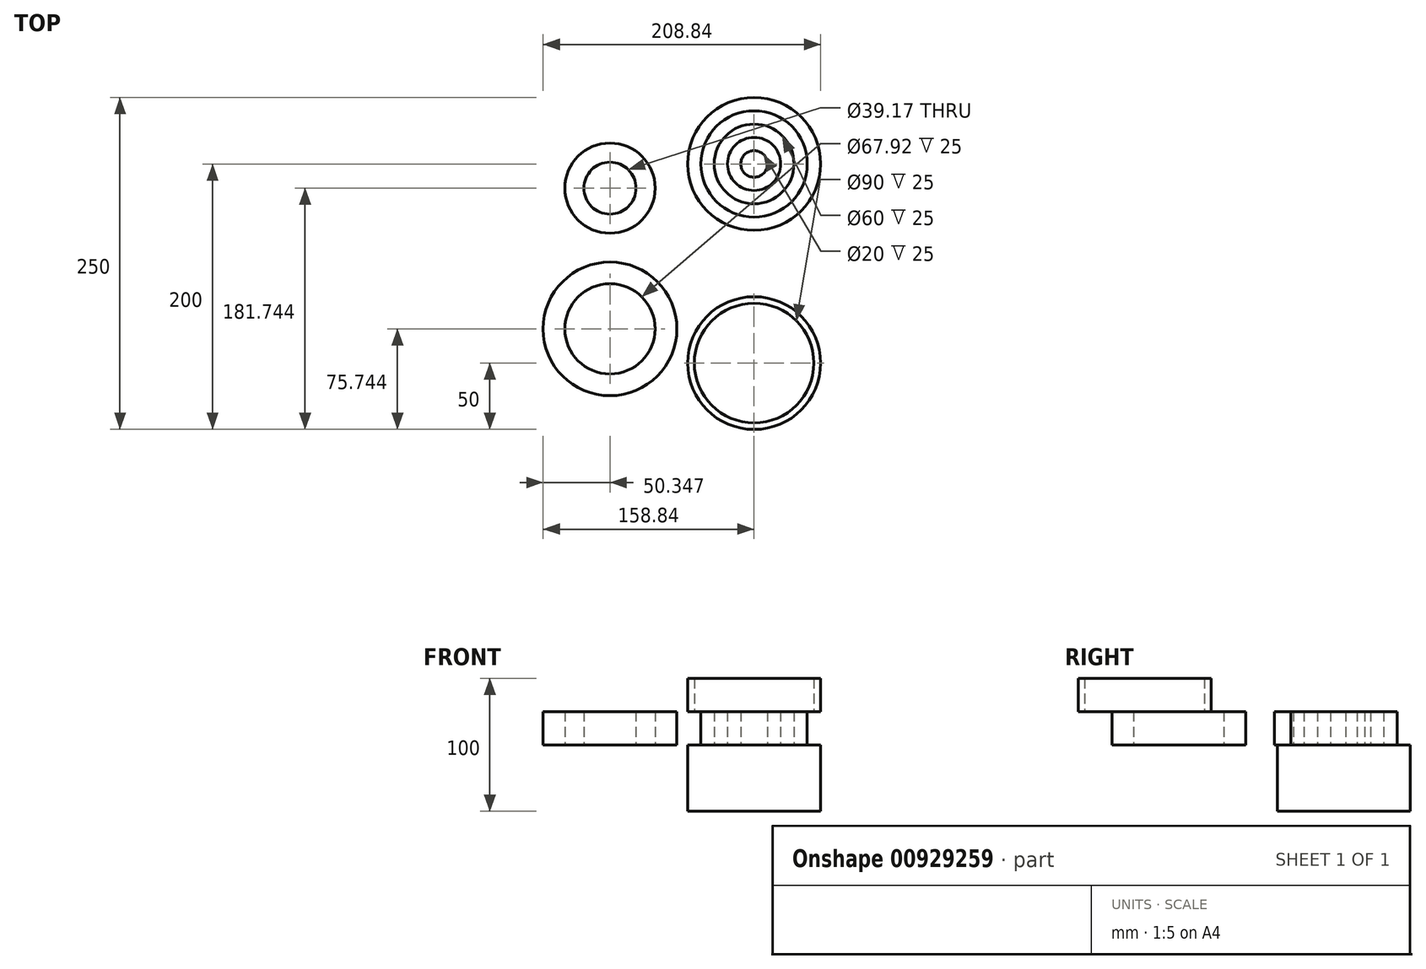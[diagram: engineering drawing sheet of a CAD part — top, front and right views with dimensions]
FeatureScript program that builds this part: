
annotation { "Feature Type Name" : "Feature", "Feature Type Description" : "" }
export const myFeature = defineFeature(function(context is Context, id is Id, definition is map)
    precondition{}
    {
        {
            var Q0;
            Q0=qCreatedBy(makeId("Top.planeOp"),FACE);
            var sketch = newSketch(context, id + "F0", { "sketchPlane" : qUnion([Q0])});
            skCircle(sketch, "E0", {"center": v(0, 0) * mm, "radius": 50 * mm});
            skSolve(sketch);
        }
        {
            var Q0;
            Q0 = qSketchRegion(id + "F0", true);
            extrude(context, id + "F1", {"entities" : qUnion([Q0]), "oppositeDirection" : true, "depth" : 50 * mm, "offsetDistance" : 25 * mm});
        }
        {
            var Q0;
            Q0=qCreatedBy(makeId("Top.planeOp"),FACE);
            var sketch = newSketch(context, id + "F2", { "sketchPlane" : qUnion([Q0])});
            skCircle(sketch, "E1", {"center": v(0, 0) * mm, "radius": 40 * mm});
            skCircle(sketch, "E2", {"center": v(0, 0) * mm, "radius": 30 * mm});
            skCircle(sketch, "E3", {"center": v(0, 0) * mm, "radius": 20 * mm});
            skCircle(sketch, "E4", {"center": v(0, 0) * mm, "radius": 10 * mm});
            skSolve(sketch);
        }
        {
            var Q0;
            Q0=makeQuery(id+"F2.imprint","IMPRINT",FACE,{"disambiguationData":[TD([[makeQuery(id+"F2.imprint","IMPRINT",EDGE,{"derivedFrom":sQuery(id+"F2.wireOp",EDGE,"E1")}),1.0]])]});
            var Q1;
            Q1=makeQuery(id+"F2.imprint","IMPRINT",FACE,{"disambiguationData":[TD([[makeQuery(id+"F2.imprint","IMPRINT",EDGE,{"derivedFrom":sQuery(id+"F2.wireOp",EDGE,"E3")}),1.0]])]});
            extrude(context, id + "F3", {"entities" : qUnion([Q0, Q1]), "operationType" : NewBodyOperationType.ADD, "depth" : 25 * mm, "offsetDistance" : 25 * mm});
        }
        {
            var Q0;
            Q0=makeQuery(id+"F3.opExtrude","CAP_FACE",FACE,{"disambiguationData":[OSD([sQuery(id+"F2.wireOp",EDGE,"E1"),sQuery(id+"F2.wireOp",EDGE,"E2")])],"isStart":false});
            var sketch = newSketch(context, id + "F4", { "sketchPlane" : qUnion([Q0])});
            skCircle(sketch, "E5.0", {"center": v(0, 0) * mm, "radius": 45 * mm});
            skCircle(sketch, "E6.0", {"center": v(0, 0) * mm, "radius": 50 * mm});
            skSolve(sketch);
        }
        {
            var Q0;
            Q0 = qSketchRegion(id + "F4", true);
            extrude(context, id + "F5", {"entities" : qUnion([Q0]), "depth" : 25 * mm, "offsetDistance" : 25 * mm});
        }
        {
            var Q0;
            Q0=qCreatedBy(makeId("Top.planeOp"),FACE);
            var sketch = newSketch(context, id + "F6", { "sketchPlane" : qUnion([Q0])});
            skCircle(sketch, "E7", {"center": v(-108.5, -124.26) * mm, "radius": 33.96 * mm});
            skCircle(sketch, "E8", {"center": v(-108.5, -124.26) * mm, "radius": 19.58 * mm});
            skCircle(sketch, "E9", {"center": v(-108.5, -124.26) * mm, "radius": 50.35 * mm});
            skSolve(sketch);
        }
        {
            var Q0;
            Q0=makeQuery(id+"F6.imprint","IMPRINT",FACE,{"disambiguationData":[TD([[makeQuery(id+"F6.imprint","IMPRINT",EDGE,{"derivedFrom":sQuery(id+"F6.wireOp",EDGE,"E7")}),-1.0]])]});
            extrude(context, id + "F7", {"entities" : qUnion([Q0]), "operationType" : NewBodyOperationType.ADD, "depth" : 25 * mm, "offsetDistance" : 25 * mm});
        }
        {
            var Q0;
            Q0=makeQuery(id+"F7.opExtrude","SWEPT_BODY",BODY,{"disambiguationData":[OSD([sQuery(id+"F6.wireOp",EDGE,"E7"),sQuery(id+"F6.wireOp",EDGE,"E9")])]});
            deleteBodies(context, id + "F8", {"entities" : qUnion([Q0])});
        }
        {
            var Q0;
            Q0=makeQuery(id+"F6.imprint","IMPRINT",FACE,{"disambiguationData":[TD([[makeQuery(id+"F6.imprint","IMPRINT",EDGE,{"derivedFrom":sQuery(id+"F6.wireOp",EDGE,"E7")}),1.0]])]});
            extrude(context, id + "F9", {"entities" : qUnion([Q0]), "operationType" : NewBodyOperationType.ADD, "depth" : 25 * mm, "offsetDistance" : 25 * mm});
        }
        {
            var Q0;
            Q0=makeQuery(id+"F6.imprint","IMPRINT",FACE,{"disambiguationData":[TD([[makeQuery(id+"F6.imprint","IMPRINT",EDGE,{"derivedFrom":sQuery(id+"F6.wireOp",EDGE,"E7")}),-1.0]])]});
            extrude(context, id + "F10", {"entities" : qUnion([Q0]), "depth" : 25 * mm, "offsetDistance" : 25 * mm});
        }
        {
            var Q0;
            Q0=makeQuery(id+"F9.opExtrude","SWEPT_BODY",BODY,{"disambiguationData":[OSD([sQuery(id+"F6.wireOp",EDGE,"E7"),sQuery(id+"F6.wireOp",EDGE,"E8")])]});
            transform(context, id + "F11", {"entities" : qUnion([Q0]), "transformType" : TransformType.TRANSLATION_3D, "dx" : 0 * mm, "dy" : 106 * mm, "dz" : 0 * mm, "makeCopy" : false});
        }
        {
            var Q0;
            Q0=makeQuery(id+"F5.opExtrude","SWEPT_BODY",BODY,{"disambiguationData":[OSD([sQuery(id+"F4.wireOp",EDGE,"E5.0"),sQuery(id+"F4.wireOp",EDGE,"E6.0")])]});
            transform(context, id + "F12", {"entities" : qUnion([Q0]), "transformType" : TransformType.TRANSLATION_3D, "dx" : 0 * mm, "dy" : -150 * mm, "dz" : 0 * mm, "makeCopy" : false});
        }
    });
